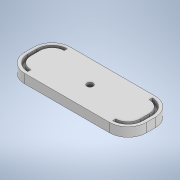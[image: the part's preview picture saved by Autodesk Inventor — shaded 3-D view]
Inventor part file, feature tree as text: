
AUTODESK INVENTOR PART (.ipt)
format: ipt  version: 2022 (Build 260153000, 153)  size: 155,648 bytes
history: native  units: mm
features: extrude x4, other x1, sketch x1, hole x1
ambient origin geometry x8: Origin, YZ Plane, XZ Plane, XY Plane, X Axis, Y Axis, Z Axis, Center Point
bodies: Body1 (feature_tree)
feature tree (7):
  other  "Sólido1"
  sketch  "Boceto1"  dims[d16=15.0mm d17=0.0mm d18=15.0mm d19=0.0mm d20=30.0mm d21=0.0mm d22=10.0mm d23=0.0mm d24=3.0mm d25=6.0mm d26=4.0mm d27=2.0mm d28=90.0deg d29=8.0mm d30=20.594885mm d32=400.0mm d33=150.0mm d31=0.75mm d34=0.75mm d35=0.375mm]
  extrude  "Extrusión1"  Depth=15.0mm TaperAngle=0.0deg
  extrude  "Extrusión2"  Depth=30.0mm TaperAngle=0.0deg
  extrude  "Extrusión3"  Depth=10.0mm TaperAngle=0.0deg
  extrude  "Extrusión4"  Depth=400.0mm
  hole  "Agujero1"  [1 undecoded]
note: 1 required parameter value undecoded (feature->parameter linkage not recoverable at this tier; creation-order binding heuristic only, values carry confidence <= 0.55)
